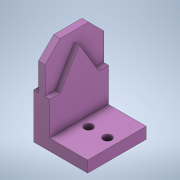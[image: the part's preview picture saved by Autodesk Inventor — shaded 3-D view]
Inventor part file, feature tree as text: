
AUTODESK INVENTOR PART (.ipt)
format: ipt  version: 2022 (Build 260153000, 153)  size: 192,000 bytes
history: native  units: in
note: dims shown in document units (in); Inventor stores cm internally (conversion verified against a paired STEP export)
features: sketch x6, extrude x5, mirror x3, other x3, projected_geometry x2, chamfer x1
ambient origin geometry x8: Origin, YZ Plane, XZ Plane, XY Plane, X Axis, Y Axis, Z Axis, Center Point
bodies: Solid1 (feature_tree)
feature tree (20):
  extrude  "Extrusion1"  Depth=0.8858in
  extrude  "Extrusion4"  Depth=0.1378in
  mirror  "Mirror2"
  extrude  "Extrusion5"  Depth=0.0984in TaperAngle=0.0deg
  extrude  "Extrusion6"  Depth=0.3937in TaperAngle=0.0deg
  mirror  "Mirror3"
  mirror  "Mirror4"
  sketch  "Sketch9"  dims[d40=0.1575in]
  other  "Work Point4"
  other  "Work Point5"
  other  "Work Point6"
  chamfer  "Chamfer1"  Distance=0.315in Angle=45.0deg
  extrude  "Extrusion7"  Depth=0.7874in
  sketch  "Sketch1"  dims[d0=1.2205in d1=0.8858in]
  sketch  "Sketch2"  dims[d2=0.1378in d3=0.0in d31=0.8067in]
  sketch  "Sketch7"  dims[d33=0.6723in d34=0.0984in d35=0.0in]
  projected_geometry  "Projected Loop2"
  sketch  "Sketch8"  dims[d36=0.9449in d37=0.0in d38=0.3937in d39=0.0in]
  projected_geometry  "Projected Loop3"
  sketch  "Sketch10"  dims[d50=0.3937in d60=0.315in d61=0.0787in d62=45.0deg d63=0.7874in d64=0.1772in d65=0.3937in d66=0.2362in d67=0.0in d68=0.0344in d69=0.0197in d70=0.0344in]
